# Revit family: Door-Folding-Kolbe-VistaLuxe_Complementary_Folding_Door
name_source: partatom
category: Doors
revit_build: Autodesk Revit 2015 (Build: 20140606_1530(x64)
units: mm (PartAtom-declared; Revit-internal decimal feet)

## types (1)
- Complementary Folding Door
    Acoustic Performance Data URL = http://www.kolbe-kolbe.com
    Air Water Structural Impact URL = http://www.kolbe-kolbe.com
    Description = Folding Door
    Divided Lites = Yes
    Ext Finish = Aluminum - Kolbe and Kolbe - Slate
    Function = Interior
    Glazing Finish = Glass - Kolbe and Kolbe - Transparent
    Height = 10' - 0"
    Horizontal Mullions = 5
    Installation Services URL = http://www.kolbe-kolbe.com
    Int Finish = Wood - Kolbe and Kolbe - Pine
    Manufacturer = Kolbe and Kolbe Millwork
    Max Panel Height = 9' - 7 73/128"
    Model = VLFD
    Panel Height = 9' - 7 73/128"
    Product Page URL = http://www.kolbe-kolbe.com
    Product data url = https://bimobject.com
    Rough Height = 9' - 9 73/256"
    Rough Width = 11' - 8 115/128"
    Sill Finish = Aluminum - Kolbe and Kolbe - Bronze Anodized - Sill Finish
    Thickness = 0' - 2 21/64"
    URL = http://www.kolbe-kolbe.com
    Vertical Mullions = 2
    Wall Closure = By host
    Warranty URL = http://www.kolbe-kolbe.com
    Width = 12' - 0"

## geometry (parser evidence)
native form markers: Blend x35, Sweep x22
no freeform markers — native parametric forms only
